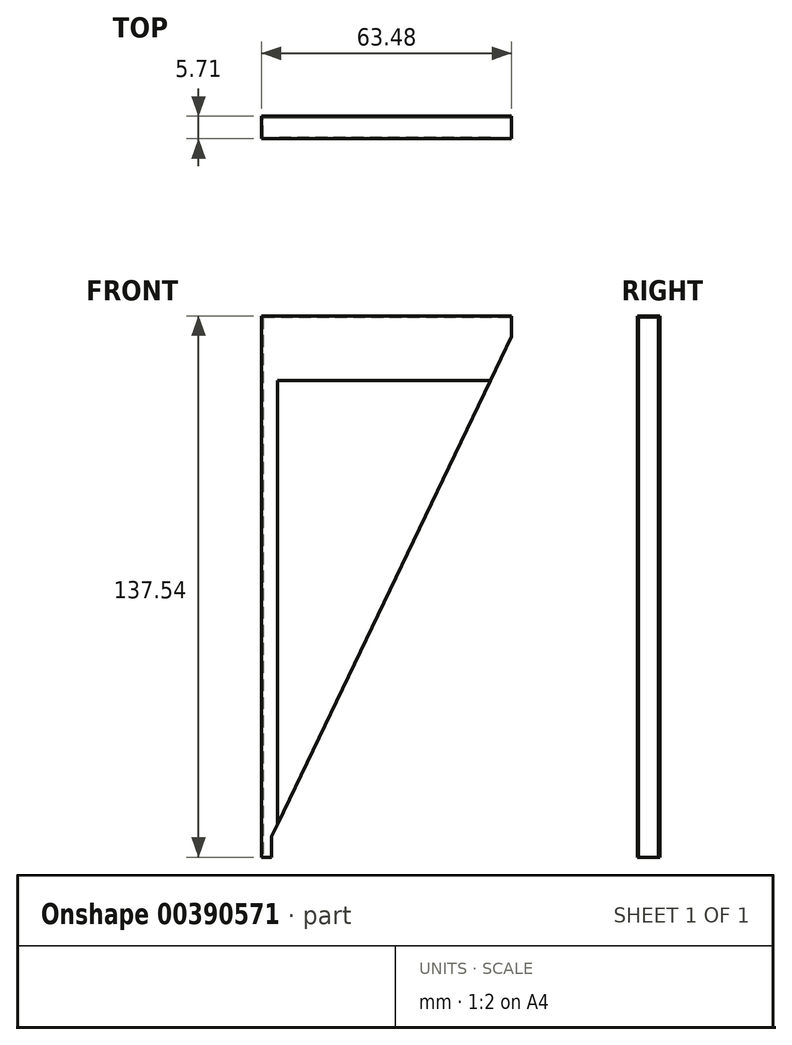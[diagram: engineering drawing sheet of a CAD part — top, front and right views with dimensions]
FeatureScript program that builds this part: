
annotation { "Feature Type Name" : "Feature", "Feature Type Description" : "" }
export const myFeature = defineFeature(function(context is Context, id is Id, definition is map)
    precondition{}
    {
        {
            var Q0;
            Q0=qCreatedBy(makeId("Front.planeOp"),FACE);
            var sketch = newSketch(context, id + "F0", { "sketchPlane" : qUnion([Q0])});
            skLineSegment(sketch, "E0.top", {"start": v(-33.17, 68.77) * mm, "end": v(30.31, 68.77) * mm});
            skLineSegment(sketch, "E0.left", {"start": v(-33.17, -68.77) * mm, "end": v(-33.17, 68.77) * mm});
            skLineSegment(sketch, "E1", {"start": v(-30.63, -63.48) * mm, "end": v(30.31, 63.5) * mm});
            skLineSegment(sketch, "E2", {"start": v(-33.17, -68.77) * mm, "end": v(-30.63, -68.77) * mm});
            skLineSegment(sketch, "E3", {"start": v(-30.63, -68.77) * mm, "end": v(-30.63, -63.48) * mm});
            skLineSegment(sketch, "E4", {"start": v(30.31, 68.77) * mm, "end": v(30.31, 63.5) * mm});
            skSolve(sketch);
        }
        {
            var Q0;
            Q0 = qSketchRegion(id + "F0", true);
            extrude(context, id + "F1", {"entities" : qUnion([Q0]), "depth" : 5.7 * mm});
        }
        {
            var Q0;
            Q0=makeQuery(id+"F1.opExtrude","CAP_FACE",FACE,{"disambiguationData":[OSD([sQuery(id+"F0.wireOp",EDGE,"E0.top"),sQuery(id+"F0.wireOp",EDGE,"E0.left"),sQuery(id+"F0.wireOp",EDGE,"E1"),sQuery(id+"F0.wireOp",EDGE,"E2"),sQuery(id+"F0.wireOp",EDGE,"E3"),sQuery(id+"F0.wireOp",EDGE,"E4")])],"isStart":false});
            var sketch = newSketch(context, id + "F2", { "sketchPlane" : qUnion([Q0])});
            skLineSegment(sketch, "E5.bottom", {"start": v(-29.18, 52.29) * mm, "end": v(24.93, 52.29) * mm});
            skLineSegment(sketch, "E5.left", {"start": v(-29.18, 52.29) * mm, "end": v(-29.18, -60.45) * mm});
            skLineSegment(sketch, "E6", {"start": v(24.93, 52.29) * mm, "end": v(-29.18, -60.45) * mm});
            skSolve(sketch);
        }
        {
            var Q0;
            Q0 = qSketchRegion(id + "F2", true);
            extrude(context, id + "F3", {"entities" : qUnion([Q0]), "operationType" : NewBodyOperationType.REMOVE, "oppositeDirection" : true, "depth" : 5.4 * mm});
        }
        {
            var Q0;
            Q0=makeQuery(id+"F1.opExtrude","SWEPT_FACE",FACE,{"disambiguationData":[OSD([sQuery(id+"F0.wireOp",EDGE,"E4")])]});
            var sketch = newSketch(context, id + "F4", { "sketchPlane" : qUnion([Q0])});
            skLineSegment(sketch, "E7.bottom", {"start": v(-5.4, 68.45) * mm, "end": v(-0.32, 68.45) * mm});
            skLineSegment(sketch, "E7.top", {"start": v(-5.4, -68.77) * mm, "end": v(-0.32, -68.77) * mm});
            skLineSegment(sketch, "E7.left", {"start": v(-5.4, 68.45) * mm, "end": v(-5.4, -68.77) * mm});
            skLineSegment(sketch, "E7.right", {"start": v(-0.32, 68.45) * mm, "end": v(-0.32, -68.77) * mm});
            skSolve(sketch);
        }
        {
            var Q0;
            Q0 = qSketchRegion(id + "F4", true);
            extrude(context, id + "F5", {"entities" : qUnion([Q0]), "operationType" : NewBodyOperationType.REMOVE, "oppositeDirection" : true, "depth" : 63.17 * mm});
        }
    });
